# Revit family: Toilet-Floor_Mount-KOHLER-Karing-K-77780
name_source: partatom
category: Plumbing Fixtures
revit_build: Autodesk Revit 2015 (Build: 20140606_1530(x64)
units: mm (PartAtom-declared; Revit-internal decimal feet)

## types (1)
- 0-White
    ADA Compliant = No
    Apparent Load = 1800 VA
    Assembly Code = D2010100
    CW Connection = Yes
    Cold Water Inlet = Cold Water Inlet
    Date Modified = 02/19/2019
    Default Elevation = 0"
    Description = 2.0 intelligent skirted one-piece elongated toilet
    Electrical Connector = Yes
    Electrical Note = One dedicated circuit required, protected with Class A Ground-Fault Circuit-Interrupter (GFCI) or Residual Current Device (RCD)
    Finish = Kohler-Vitreous_China-0-White
    Flow Rate = 0 GPM
    Flush Rate = 1.08GPF
    HW Connection = No
    Height = 20 13/16"
    Hot Water Inlet = Hot Water Inlet
    Length = 27 3/4"
    Manufacturer = KOHLER Co.
    MasterFormat 1995 = 15410
    MasterFormat 2004 = 22.41.13
    Material = Vitreous China
    Model = K-77780-0
    Pressure = 20.00 psi
    Product Documentation Link = https://www.us.kohler.com
    Product Name = Karing
    Product Page URL = http://www.us.kohler.com
    Rough-In = 12"
    Seat Included = Yes
    URL = https://www.us.kohler.com
    Vent Connection = No
    Voltage = 120 V
    Waste Connection = Yes
    Waste Water Outlet = Waste Water Outlet
    WaterSense Certified = Yes
    Width = 17 3/4"

## geometry (parser evidence)
native form markers: Sweep x5
no freeform markers — native parametric forms only
